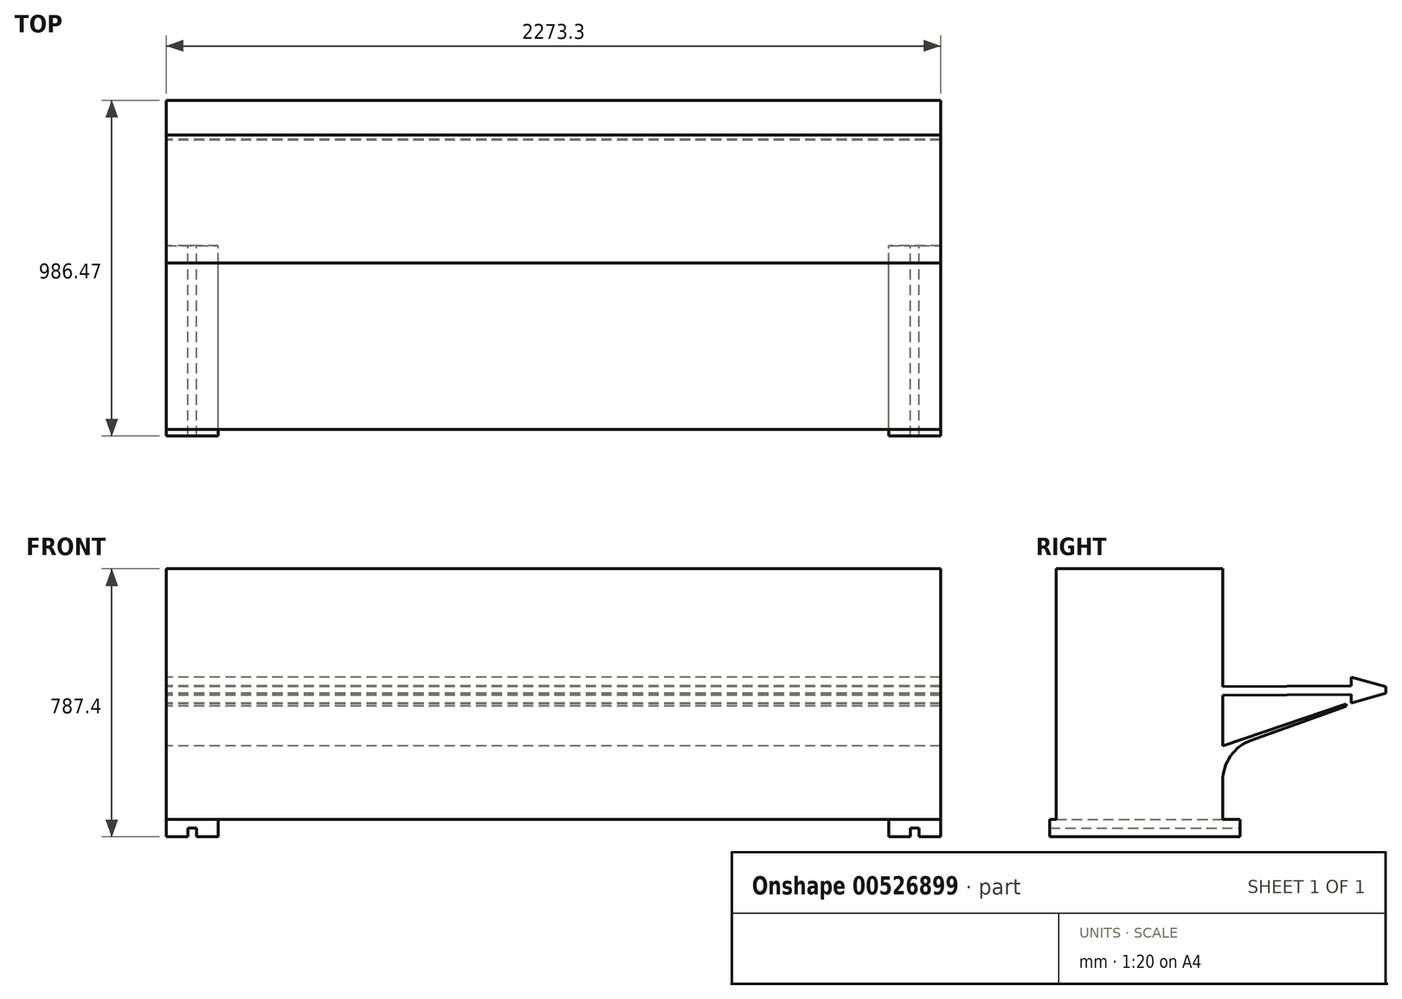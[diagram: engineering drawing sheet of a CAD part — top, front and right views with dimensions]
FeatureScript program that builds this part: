
annotation { "Feature Type Name" : "Feature", "Feature Type Description" : "" }
export const myFeature = defineFeature(function(context is Context, id is Id, definition is map)
    precondition{}
    {
        {
            var Q0;
            Q0=qCreatedBy(makeId("Right.planeOp"),FACE);
            var sketch = newSketch(context, id + "F0", { "sketchPlane" : qUnion([Q0])});
            skLineSegment(sketch, "E0", {"start": v(-488.95, 0) * mm, "end": v(-488.95, 736.6) * mm});
            skLineSegment(sketch, "E1", {"start": v(-488.95, 736.6) * mm, "end": v(0, 736.6) * mm});
            skLineSegment(sketch, "E2", {"start": v(0, 378.3) * mm, "end": v(0, 736.6) * mm});
            skLineSegment(sketch, "E3", {"start": v(-488.95, 0) * mm, "end": v(0, 0) * mm});
            skLineSegment(sketch, "E4", {"start": v(478.38, 380.37) * mm, "end": v(0, 378.3) * mm, "construction": true});
            skPoint(sketch, "E5", {"position": v(478.38, 389.9) * mm});
            skLineSegment(sketch, "E6", {"start": v(478.38, 389.9) * mm, "end": v(478.38, 380.37) * mm});
            skLineSegment(sketch, "E7.MirrorCS", {"start": v(478.47, 370.84) * mm, "end": v(478.38, 380.37) * mm});
            skLineSegment(sketch, "E8", {"start": v(478.38, 380.37) * mm, "end": v(376.78, 379.93) * mm});
            skLineSegment(sketch, "E9", {"start": v(376.78, 379.93) * mm, "end": v(376.62, 418.03) * mm});
            skLineSegment(sketch, "E10", {"start": v(376.62, 418.03) * mm, "end": v(478.38, 389.9) * mm});
            skLineSegment(sketch, "E11.MirrorCS", {"start": v(376.78, 379.93) * mm, "end": v(376.95, 341.83) * mm});
            skLineSegment(sketch, "E12.MirrorCS", {"start": v(376.95, 341.83) * mm, "end": v(478.47, 370.84) * mm});
            skLineSegment(sketch, "E13", {"start": v(0, 378.3) * mm, "end": v(0, 391) * mm});
            skLineSegment(sketch, "E14", {"start": v(0, 391) * mm, "end": v(376.73, 392.63) * mm});
            skLineSegment(sketch, "E15.MirrorCS", {"start": v(0.1, 365.6) * mm, "end": v(376.84, 367.23) * mm});
            skLineSegment(sketch, "E16", {"start": v(0.1, 365.6) * mm, "end": v(0, 378.3) * mm});
            skLineSegment(sketch, "E17", {"start": v(0, 215.9) * mm, "end": v(0.1, 365.6) * mm});
            skPoint(sketch, "E18.visualSharp", {"position": v(0, 203.2) * mm});
            skLineSegment(sketch, "E19", {"start": v(0, 0) * mm, "end": v(0, 113.83) * mm});
            skLineSegment(sketch, "E20", {"start": v(84.13, 233.37) * mm, "end": v(363.63, 333.6) * mm});
            skLineSegment(sketch, "E21", {"start": v(363.63, 333.6) * mm, "end": v(361.49, 339.58) * mm});
            skLineSegment(sketch, "E22", {"start": v(361.49, 339.58) * mm, "end": v(0, 215.9) * mm});
            skArc(sketch, "E23.filletArc", {"start": v(84.13, 233.37) * mm, "mid": v(23.14, 186.92) * mm, "end": v(0, 113.83) * mm});
            skSolve(sketch);
        }
        {
            var Q0;
            Q0 = qSketchRegion(id + "F0", true);
            extrude(context, id + "F1", {"entities" : qUnion([Q0]), "depth" : 2273.3 * mm, "offsetDistance" : 25.4 * mm});
        }
        {
            var Q0;
            Q0=qCreatedBy(makeId("Front.planeOp"),FACE);
            var sketch = newSketch(context, id + "F2", { "sketchPlane" : qUnion([Q0])});
            skLineSegment(sketch, "E24", {"start": v(0, 0) * mm, "end": v(76.2, 0) * mm});
            skLineSegment(sketch, "E25", {"start": v(76.2, 0) * mm, "end": v(152.4, 0) * mm});
            skLineSegment(sketch, "E26", {"start": v(152.4, 0) * mm, "end": v(152.4, -50.8) * mm});
            skLineSegment(sketch, "E27", {"start": v(152.4, -50.8) * mm, "end": v(88.9, -50.8) * mm});
            skLineSegment(sketch, "E28", {"start": v(88.9, -50.8) * mm, "end": v(88.9, -25.4) * mm});
            skLineSegment(sketch, "E29", {"start": v(88.9, -25.4) * mm, "end": v(63.5, -25.4) * mm});
            skLineSegment(sketch, "E30", {"start": v(63.5, -25.4) * mm, "end": v(63.5, -50.8) * mm});
            skLineSegment(sketch, "E31", {"start": v(0, -50.8) * mm, "end": v(0, 0) * mm});
            skLineSegment(sketch, "E32", {"start": v(63.5, -50.8) * mm, "end": v(0, -50.8) * mm});
            skLineSegment(sketch, "E33", {"start": v(1136.65, 0) * mm, "end": v(1136.65, 735.11) * mm});
            skLineSegment(sketch, "E34.MirrorCS", {"start": v(2273.3, 0) * mm, "end": v(2197.1, 0) * mm});
            skLineSegment(sketch, "E35.MirrorCS", {"start": v(2197.1, 0) * mm, "end": v(2120.9, 0) * mm});
            skLineSegment(sketch, "E36.MirrorCS", {"start": v(2120.9, 0) * mm, "end": v(2120.9, -50.8) * mm});
            skLineSegment(sketch, "E37.MirrorCS", {"start": v(2120.9, -50.8) * mm, "end": v(2184.4, -50.8) * mm});
            skLineSegment(sketch, "E38.MirrorCS", {"start": v(2184.4, -50.8) * mm, "end": v(2184.4, -25.4) * mm});
            skLineSegment(sketch, "E39.MirrorCS", {"start": v(2184.4, -25.4) * mm, "end": v(2209.8, -25.4) * mm});
            skLineSegment(sketch, "E40.MirrorCS", {"start": v(2209.8, -25.4) * mm, "end": v(2209.8, -50.8) * mm});
            skLineSegment(sketch, "E41.MirrorCS", {"start": v(2209.8, -50.8) * mm, "end": v(2273.3, -50.8) * mm});
            skLineSegment(sketch, "E42.MirrorCS", {"start": v(2273.3, -50.8) * mm, "end": v(2273.3, 0) * mm});
            skSolve(sketch);
        }
        {
            var Q0;
            Q0 = qSketchRegion(id + "F2", true);
            extrude(context, id + "F3", {"entities" : qUnion([Q0]), "operationType" : NewBodyOperationType.ADD, "depth" : 508 * mm, "offsetDistance" : 25.4 * mm, "hasSecondDirection" : true, "secondDirectionOppositeDirection" : true, "secondDirectionDepth" : 50.8 * mm});
        }
    });
